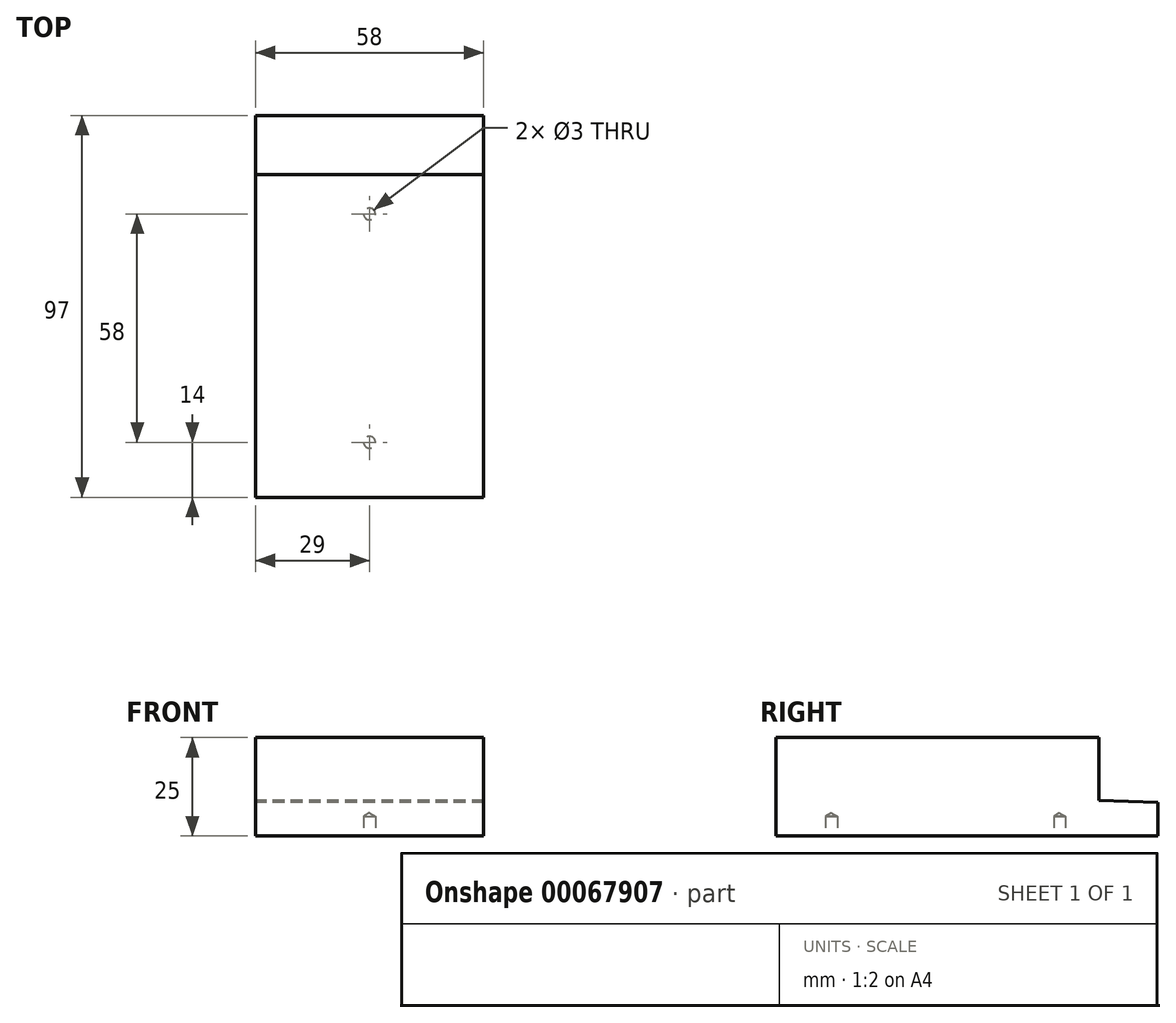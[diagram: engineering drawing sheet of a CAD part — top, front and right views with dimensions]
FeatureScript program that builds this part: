
annotation { "Feature Type Name" : "Feature", "Feature Type Description" : "" }
export const myFeature = defineFeature(function(context is Context, id is Id, definition is map)
    precondition{}
    {
        {
            var Q0;
            Q0=qCreatedBy(makeId("Right.planeOp"),FACE);
            var sketch = newSketch(context, id + "F0", { "sketchPlane" : qUnion([Q0])});
            skLineSegment(sketch, "E0.bottom", {"start": v(0, 0) * mm, "end": v(97, 0) * mm});
            skLineSegment(sketch, "E0.top", {"start": v(0, 25) * mm, "end": v(82, 25) * mm});
            skLineSegment(sketch, "E0.left", {"start": v(0, 0) * mm, "end": v(0, 25) * mm});
            skLineSegment(sketch, "E0.right", {"start": v(97, 0) * mm, "end": v(97, 8.5) * mm});
            skLineSegment(sketch, "E1", {"start": v(82, 25) * mm, "end": v(82, 9) * mm});
            skLineSegment(sketch, "E2", {"start": v(97, 8.5) * mm, "end": v(82, 9) * mm});
            skSolve(sketch);
        }
        {
            var Q0;
            Q0=makeQuery(id+"F0.imprint","IMPRINT",FACE,{"disambiguationData":[TD([[makeQuery(id+"F0.imprint","IMPRINT",EDGE,{"derivedFrom":sQuery(id+"F0.wireOp",EDGE,"E0.bottom")}),1.0]])]});
            extrude(context, id + "F1", {"entities" : qUnion([Q0]), "endBound" : BoundingType.SYMMETRIC, "depth" : 58 * mm});
        }
        {
            var Q0;
            Q0=qCreatedBy(makeId("Top.planeOp"),FACE);
            var sketch = newSketch(context, id + "F2", { "sketchPlane" : qUnion([Q0])});
            skPoint(sketch, "E3", {"position": v(0, 14) * mm});
            skPoint(sketch, "E4", {"position": v(0, 72) * mm});
            skSolve(sketch);
        }
        {
            var Q0;
            Q0=sQuery(id+"F2.wireOp",VERTEX,"E3");
            var Q1;
            Q1=sQuery(id+"F2.wireOp",VERTEX,"E4");
            var Q2;
            Q2=makeQuery(id+"F1.opExtrude","SWEPT_BODY",BODY,{"disambiguationData":[OSD([sQuery(id+"F0.wireOp",EDGE,"E0.bottom"),sQuery(id+"F0.wireOp",EDGE,"E0.top"),sQuery(id+"F0.wireOp",EDGE,"E0.left"),sQuery(id+"F0.wireOp",EDGE,"E0.right")])]});
            hole(context, id + "F3", {"style" : HoleStyle.SIMPLE, "endStyle" : HoleEndStyle.BLIND, "oppositeDirection" : true, "holeDiameter" : 3 * mm, "holeDepth" : 5 * mm, "locations" : qUnion([Q0, Q1]), "scope" : qUnion([Q2])});
        }
    });
